# Revit family: QF_ELECTROLUXPROFESSIONAL_391156_E9WTNBN000
name_source: partatom
category: Specialty Equipment
revit_build: Autodesk Revit 2018 (Build: 20190510_1515(x64)
units: mm (PartAtom-declared; Revit-internal decimal feet)

## family parameters
Always vertical = Yes
Cut with Voids When Loaded = No
Part Type = Normal
Room Calculation Point = No
Round Connector Dimension = Use Diameter
Shared = No
Work Plane-Based = No

## types (1)
- QF_ELECTROLUXPROFESSIONAL_391156_E9WTNBN000
    Base Height = 24 mm  [stored 0.0787402 ft]
    Depth = 930 mm  [stored 3.05118 ft]
    Description = 900XP AMBIENT WORKTOP - 200MM
    Direct Waste Size = 0"
    Height = 289 mm  [stored 0.948163 ft]
    Manufacturer = ELECTROLUX
    Model = 391156
    URL = www.electrolux.com
    URL Cutsheet = www.electrolux.com
    Weight in Pounds = 13
    Width = 200 mm  [stored 0.656168 ft]

note: [stored X ft] marks values corroborated as IEEE doubles in the binary element streams (Revit-internal decimal feet)

## geometry (parser evidence)
native form markers: Blend x29, Sweep x2
no freeform markers — native parametric forms only
